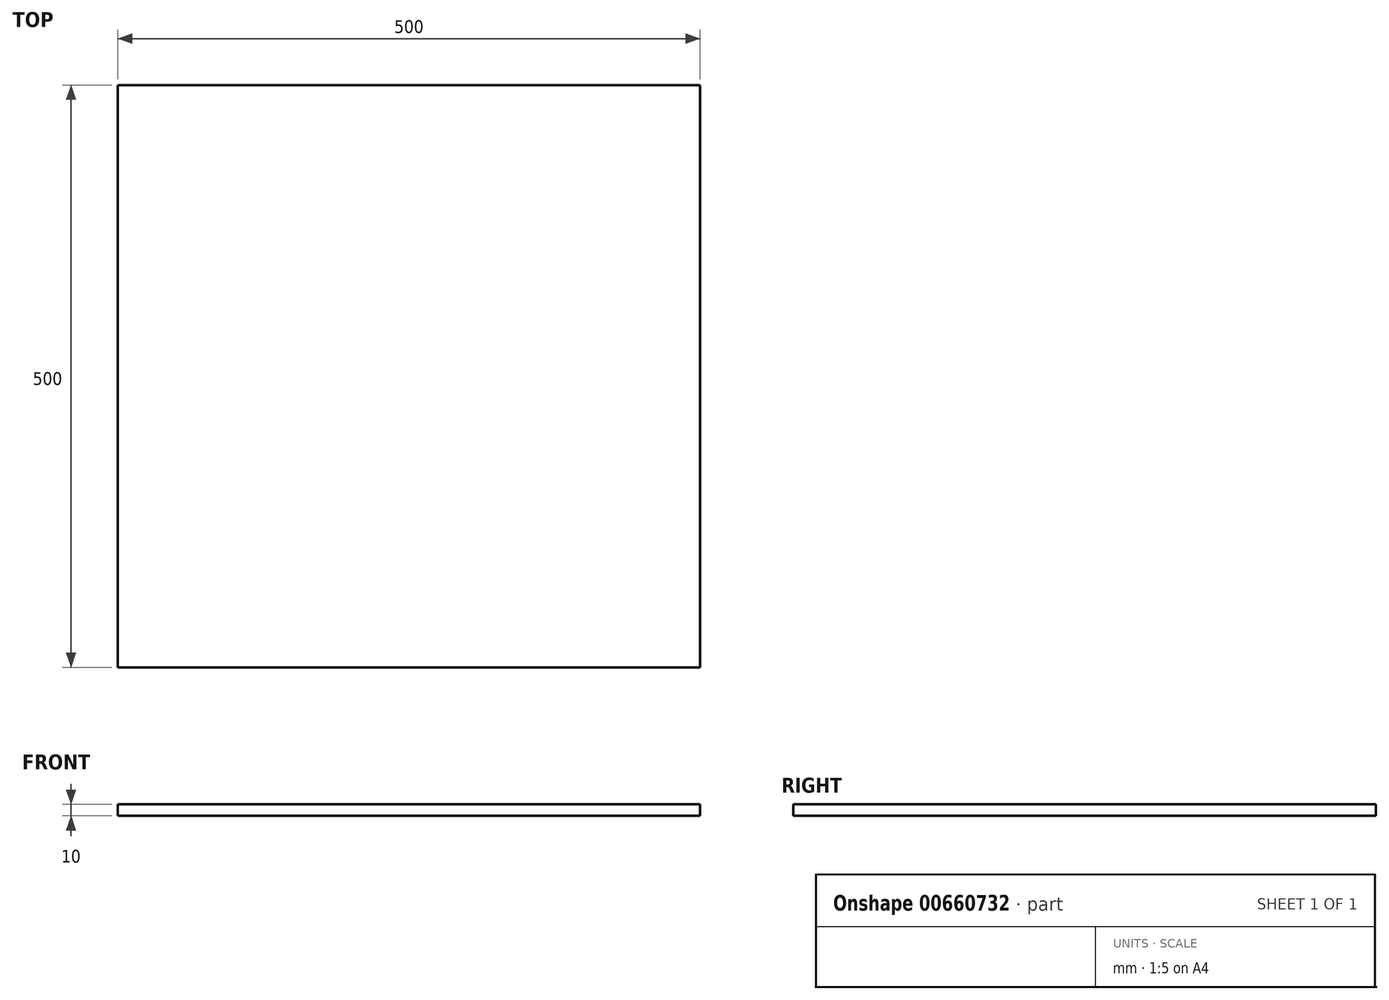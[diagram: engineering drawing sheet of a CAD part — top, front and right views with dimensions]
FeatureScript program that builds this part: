
annotation { "Feature Type Name" : "Feature", "Feature Type Description" : "" }
export const myFeature = defineFeature(function(context is Context, id is Id, definition is map)
    precondition{}
    {
        {
            var Q0;
            Q0=qCreatedBy(makeId("Top.planeOp"),FACE);
            var sketch = newSketch(context, id + "F0", { "sketchPlane" : qUnion([Q0])});
            skLineSegment(sketch, "E0.bottom", {"start": v(0, 0) * mm, "end": v(500, 0) * mm});
            skLineSegment(sketch, "E0.top", {"start": v(0, 500) * mm, "end": v(500, 500) * mm});
            skLineSegment(sketch, "E0.left", {"start": v(0, 0) * mm, "end": v(0, 500) * mm});
            skLineSegment(sketch, "E0.right", {"start": v(500, 0) * mm, "end": v(500, 500) * mm});
            skSolve(sketch);
        }
        {
            var Q0;
            Q0 = qSketchRegion(id + "F0", true);
            extrude(context, id + "F1", {"entities" : qUnion([Q0]), "depth" : 10 * mm, "offsetDistance" : 25 * mm});
        }
    });
